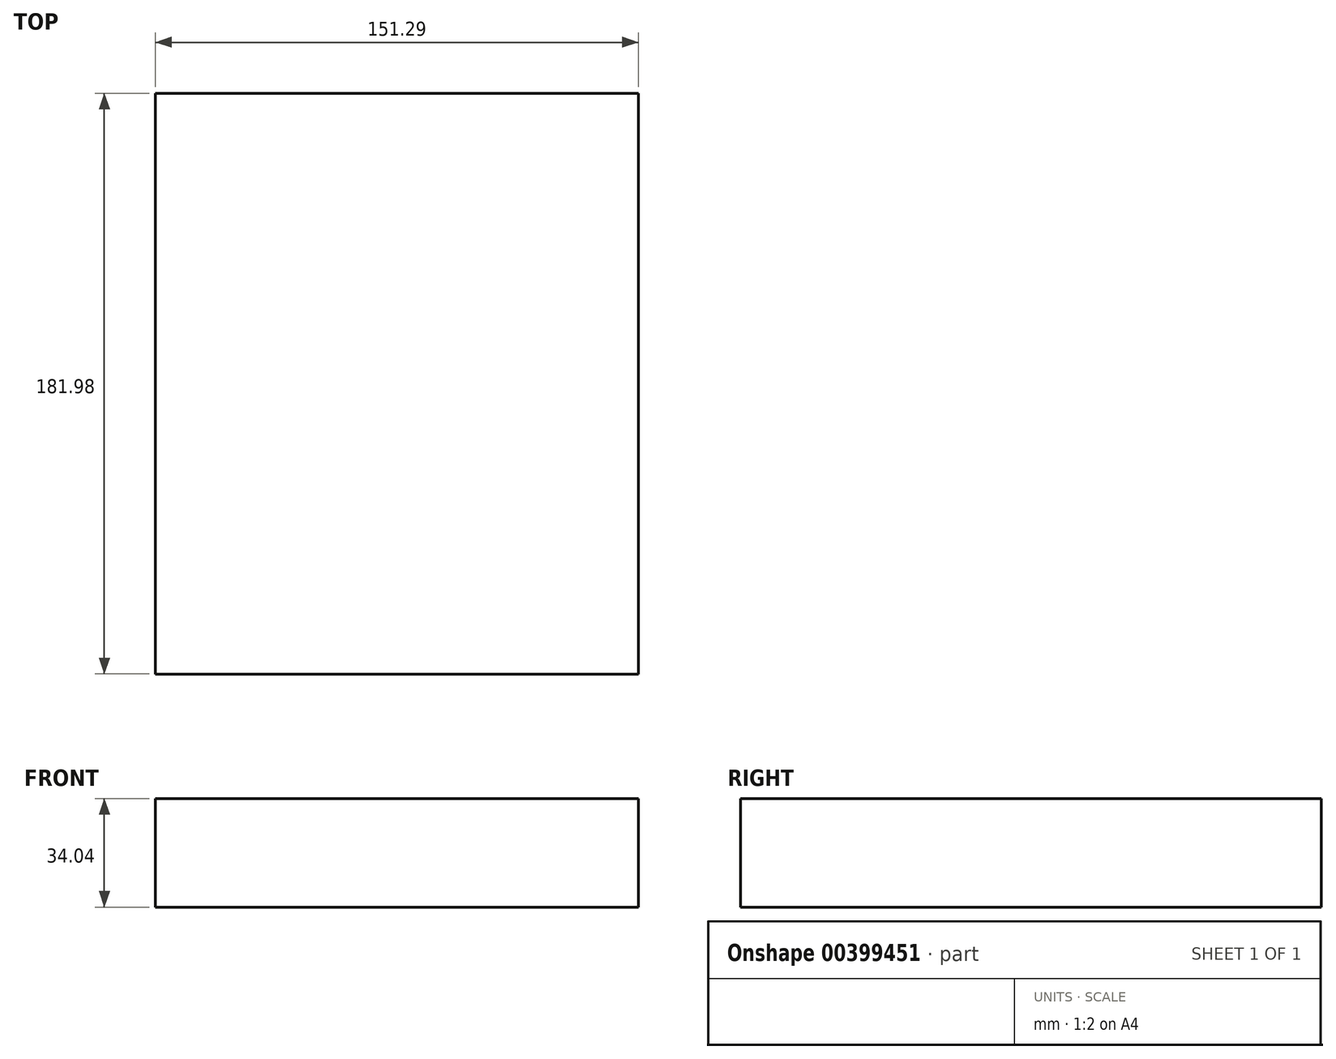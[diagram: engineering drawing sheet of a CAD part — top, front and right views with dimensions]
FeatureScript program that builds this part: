
annotation { "Feature Type Name" : "Feature", "Feature Type Description" : "" }
export const myFeature = defineFeature(function(context is Context, id is Id, definition is map)
    precondition{}
    {
        {
            var Q0;
            Q0=qCreatedBy(makeId("Top.planeOp"),FACE);
            var sketch = newSketch(context, id + "F0", { "sketchPlane" : qUnion([Q0])});
            skLineSegment(sketch, "E0.bottom", {"start": v(-120.7, -67.36) * mm, "end": v(30.59, -67.36) * mm});
            skLineSegment(sketch, "E0.top", {"start": v(-120.7, 114.62) * mm, "end": v(30.59, 114.62) * mm});
            skLineSegment(sketch, "E0.left", {"start": v(-120.7, -67.36) * mm, "end": v(-120.7, 114.62) * mm});
            skLineSegment(sketch, "E0.right", {"start": v(30.59, -67.36) * mm, "end": v(30.59, 114.62) * mm});
            skSolve(sketch);
        }
        {
            var Q0;
            Q0=makeQuery(id+"F0.imprint","IMPRINT",FACE,{"disambiguationData":[TD([[makeQuery(id+"F0.imprint","IMPRINT",EDGE,{"derivedFrom":sQuery(id+"F0.wireOp",EDGE,"E0.bottom")}),1.0]])]});
            extrude(context, id + "F1", {"entities" : qUnion([Q0]), "oppositeDirection" : true, "depth" : 34.04 * mm});
        }
    });
